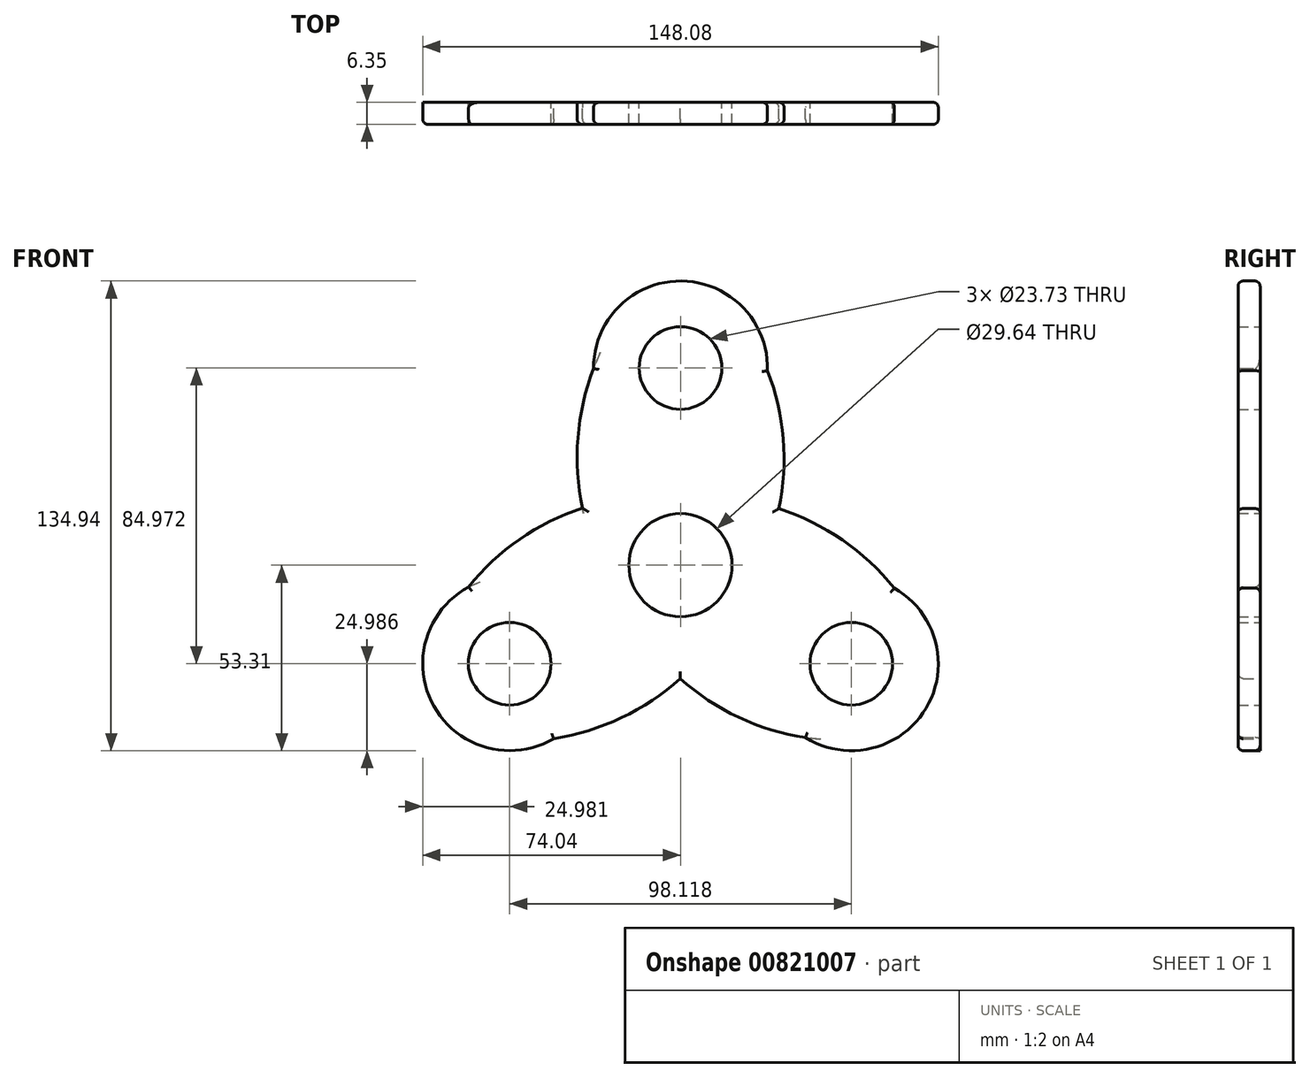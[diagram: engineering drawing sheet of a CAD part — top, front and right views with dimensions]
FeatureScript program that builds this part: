
annotation { "Feature Type Name" : "Feature", "Feature Type Description" : "" }
export const myFeature = defineFeature(function(context is Context, id is Id, definition is map)
    precondition{}
    {
        {
            var Q0;
            Q0=qCreatedBy(makeId("Front.planeOp"),FACE);
            var sketch = newSketch(context, id + "F0", { "sketchPlane" : qUnion([Q0])});
            skCircle(sketch, "E0", {"center": v(0, 0) * mm, "radius": 14.82 * mm});
            skCircle(sketch, "E1", {"center": v(0, 56.65) * mm, "radius": 11.86 * mm});
            skArc(sketch, "E2", {"start": v(24.97, 55.86) * mm, "mid": v(0.3, 81.63) * mm, "end": v(-24.98, 56.47) * mm});
            skArc(sketch, "E3", {"start": v(28.27, 16.24) * mm, "mid": v(29.52, 36.3) * mm, "end": v(24.97, 55.86) * mm});
            skArc(sketch, "E4", {"start": v(-24.98, 56.47) * mm, "mid": v(-29.48, 36.65) * mm, "end": v(-28.2, 16.36) * mm});
            skArc(sketch, "E5.1.0", {"start": v(-60.86, -6.3) * mm, "mid": v(-70.85, -40.55) * mm, "end": v(-36.42, -49.87) * mm});
            skArc(sketch, "E5.1.1", {"start": v(-36.42, -49.87) * mm, "mid": v(-17, -43.85) * mm, "end": v(-0.06, -32.6) * mm});
            skArc(sketch, "E5.1.2", {"start": v(-28.2, 16.36) * mm, "mid": v(-46.2, 7.42) * mm, "end": v(-60.86, -6.3) * mm});
            skCircle(sketch, "E5.1.3", {"center": v(-49.06, -28.32) * mm, "radius": 11.86 * mm});
            skArc(sketch, "E5.2.0", {"start": v(35.9, -49.56) * mm, "mid": v(70.54, -41.08) * mm, "end": v(61.4, -6.6) * mm});
            skArc(sketch, "E5.2.1", {"start": v(61.4, -6.6) * mm, "mid": v(46.47, 7.2) * mm, "end": v(28.27, 16.24) * mm});
            skArc(sketch, "E5.2.2", {"start": v(-0.06, -32.6) * mm, "mid": v(16.67, -43.71) * mm, "end": v(35.9, -49.56) * mm});
            skCircle(sketch, "E5.2.3", {"center": v(49.06, -28.32) * mm, "radius": 11.86 * mm});
            skPoint(sketch, "E6.orphan", {"position": v(-11.33, 19.62) * mm});
            skPoint(sketch, "E7.orphan", {"position": v(11.33, 19.62) * mm});
            skPoint(sketch, "E8.orphan", {"position": v(22.66, 0) * mm});
            skPoint(sketch, "E9.orphan", {"position": v(11.33, -19.62) * mm});
            skPoint(sketch, "E10.orphan", {"position": v(-22.66, 0) * mm});
            skSolve(sketch);
        }
        {
            var Q0;
            Q0 = qSketchRegion(id + "F0", true);
            extrude(context, id + "F1", {"entities" : qUnion([Q0]), "depth" : 6.35 * mm, "offsetDistance" : 25.4 * mm});
        }
        {
            var Q0;
            Q0=makeQuery(id+"F1.opExtrude","CAP_EDGE",EDGE,{"disambiguationData":[OSD([sQuery(id+"F0.wireOp",EDGE,"E2")])],"isStart":false});
            var Q1;
            Q1=makeQuery(id+"F1.opExtrude","CAP_EDGE",EDGE,{"disambiguationData":[OSD([sQuery(id+"F0.wireOp",EDGE,"E2")])],"isStart":true});
            var Q2;
            Q2=makeQuery(id+"F1.opExtrude","CAP_EDGE",EDGE,{"disambiguationData":[OSD([sQuery(id+"F0.wireOp",EDGE,"E3")])],"isStart":false});
            var Q3;
            Q3=makeQuery(id+"F1.opExtrude","CAP_EDGE",EDGE,{"disambiguationData":[OSD([sQuery(id+"F0.wireOp",EDGE,"E5.2.1")])],"isStart":false});
            var Q4;
            Q4=makeQuery(id+"F1.opExtrude","CAP_EDGE",EDGE,{"disambiguationData":[OSD([sQuery(id+"F0.wireOp",EDGE,"E3")])],"isStart":true});
            var Q5;
            Q5=makeQuery(id+"F1.opExtrude","CAP_EDGE",EDGE,{"disambiguationData":[OSD([sQuery(id+"F0.wireOp",EDGE,"E5.2.1")])],"isStart":true});
            var Q6;
            Q6=makeQuery(id+"F1.opExtrude","CAP_EDGE",EDGE,{"disambiguationData":[OSD([sQuery(id+"F0.wireOp",EDGE,"E5.2.0")])],"isStart":true});
            var Q7;
            Q7=makeQuery(id+"F1.opExtrude","CAP_EDGE",EDGE,{"disambiguationData":[OSD([sQuery(id+"F0.wireOp",EDGE,"E5.2.0")])],"isStart":false});
            var Q8;
            Q8=makeQuery(id+"F1.opExtrude","CAP_EDGE",EDGE,{"disambiguationData":[OSD([sQuery(id+"F0.wireOp",EDGE,"E5.2.2")])],"isStart":false});
            var Q9;
            Q9=makeQuery(id+"F1.opExtrude","CAP_EDGE",EDGE,{"disambiguationData":[OSD([sQuery(id+"F0.wireOp",EDGE,"E5.1.1")])],"isStart":false});
            var Q10;
            Q10=makeQuery(id+"F1.opExtrude","CAP_EDGE",EDGE,{"disambiguationData":[OSD([sQuery(id+"F0.wireOp",EDGE,"E5.1.0")])],"isStart":false});
            var Q11;
            Q11=makeQuery(id+"F1.opExtrude","CAP_EDGE",EDGE,{"disambiguationData":[OSD([sQuery(id+"F0.wireOp",EDGE,"E5.1.2")])],"isStart":false});
            var Q12;
            Q12=makeQuery(id+"F1.opExtrude","CAP_EDGE",EDGE,{"disambiguationData":[OSD([sQuery(id+"F0.wireOp",EDGE,"E4")])],"isStart":false});
            var Q13;
            Q13=makeQuery(id+"F1.opExtrude","CAP_EDGE",EDGE,{"disambiguationData":[OSD([sQuery(id+"F0.wireOp",EDGE,"E5.1.2")])],"isStart":true});
            fillet(context, id + "F2", {"entities" : qUnion([Q0, Q1, Q2, Q3, Q4, Q5, Q6, Q7, Q8, Q9, Q10, Q11, Q12, Q13]), "radius" : 1.52 * mm, "tangentPropagation" : true, "allowEdgeOverflow" : false});
        }
    });
